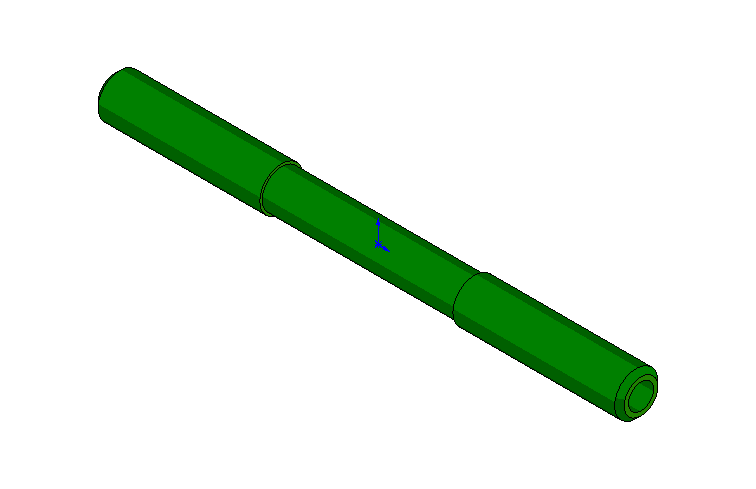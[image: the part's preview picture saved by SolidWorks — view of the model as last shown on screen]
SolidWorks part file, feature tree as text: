
SOLIDWORKS PART (.sldprt)
format: sldprt  version: not decoded by parser v0  size: 123,904 bytes
history: native  units: mm
features: plane x3, sketch x2, material x1, extrude x1, cut_extrude x1, chamfer x1 (+10 scaffold rows collapsed)
feature tree (19):
  scaffold x10  (default folders/planes/origin — collapsed)
  material  "Matériau <non spécifié>"
  plane  "Plan de face"
  plane  "Plan de dessus"
  plane  "Plan de droite"
  sketch  "Esquisse1"  dims[D1=9.0mm D2=5.2mm]
  extrude  "Extrusion1"  Depth=109mm
  sketch  "Esquisse2"  dims[D1=8.0mm]
  cut_extrude  "Enlèv. mat.-Extru.1"  Depth=40mm
  chamfer  "Chanfrein1"  Distance=1mm Angle=45deg
decode coverage: 5 of 5 modeling features carry decoded parameters
note: suppression state not decoded; provenance and decode notes live in map.json
